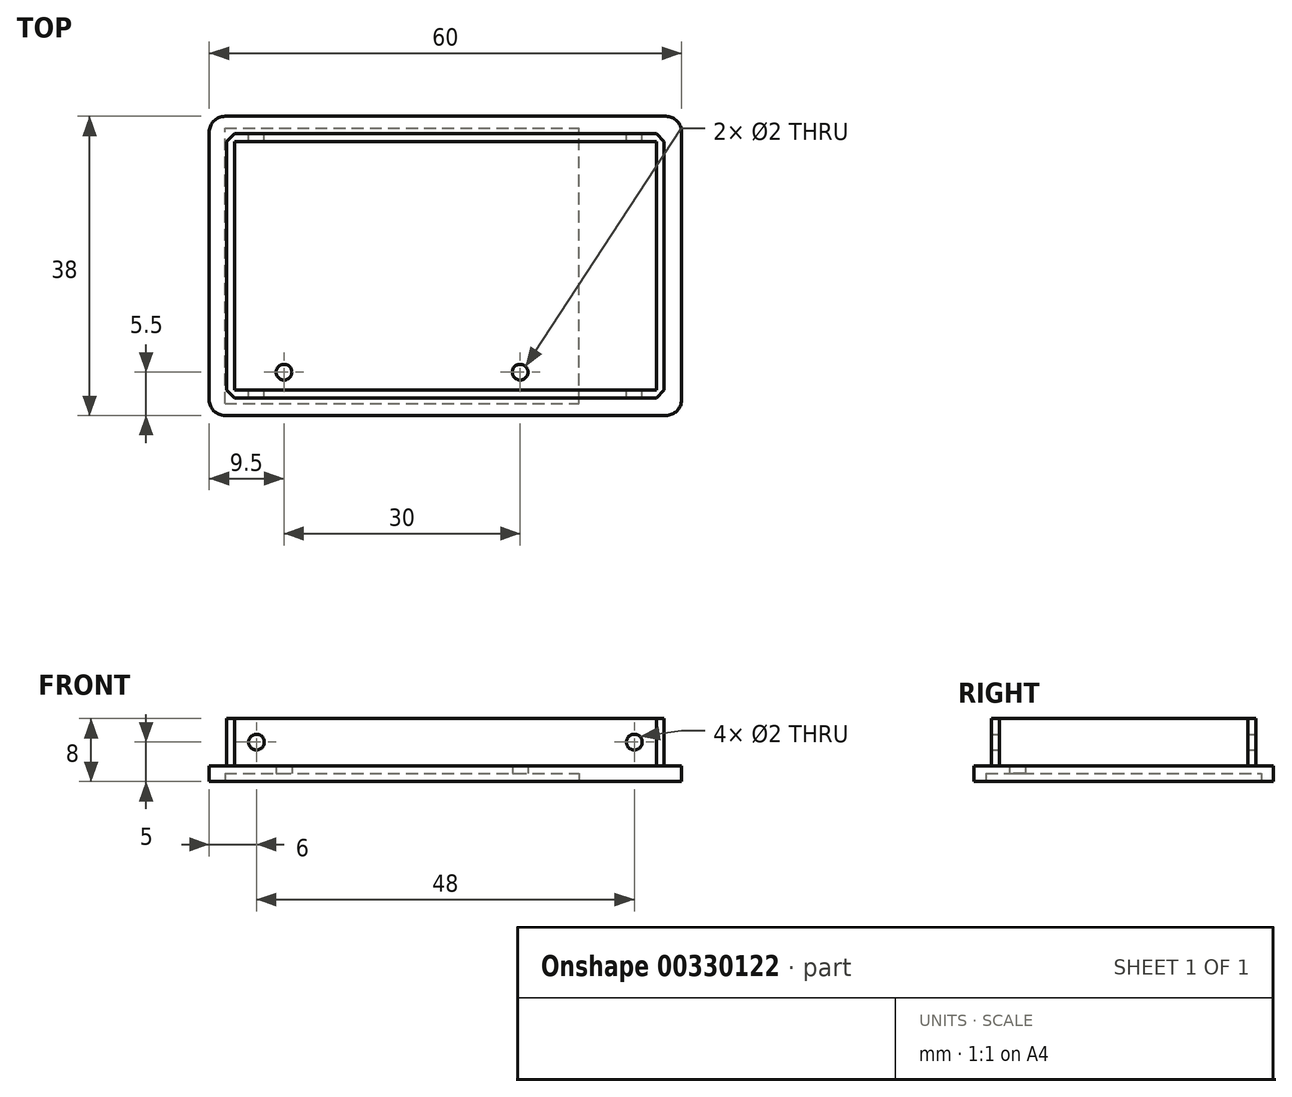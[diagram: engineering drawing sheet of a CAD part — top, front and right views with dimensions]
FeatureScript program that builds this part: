
annotation { "Feature Type Name" : "Feature", "Feature Type Description" : "" }
export const myFeature = defineFeature(function(context is Context, id is Id, definition is map)
    precondition{}
    {
        {
            var Q0;
            Q0=qCreatedBy(makeId("Top.planeOp"),FACE);
            var sketch = newSketch(context, id + "F0", { "sketchPlane" : qUnion([Q0])});
            skLineSegment(sketch, "E0.bottom", {"start": v(0, 0) * mm, "end": v(60, 0) * mm});
            skLineSegment(sketch, "E0.top", {"start": v(0, -38) * mm, "end": v(60, -38) * mm});
            skLineSegment(sketch, "E0.left", {"start": v(0, 0) * mm, "end": v(0, -38) * mm});
            skLineSegment(sketch, "E0.right", {"start": v(60, 0) * mm, "end": v(60, -38) * mm});
            skSolve(sketch);
        }
        {
            var Q0;
            Q0=qSketchRegion(id+"F0",true);
            extrude(context, id + "F1", {"entities" : qUnion([Q0]), "depth" : 2 * mm});
        }
        {
            var Q0;
            Q0=makeQuery(id+"F1.opExtrude","CAP_FACE",FACE,{"disambiguationData":[OSD([sQuery(id+"F0.wireOp",EDGE,"E0.bottom"),sQuery(id+"F0.wireOp",EDGE,"E0.top"),sQuery(id+"F0.wireOp",EDGE,"E0.left"),sQuery(id+"F0.wireOp",EDGE,"E0.right")])],"isStart":false});
            var sketch = newSketch(context, id + "F2", { "sketchPlane" : qUnion([Q0])});
            skLineSegment(sketch, "E1.bottom", {"start": v(2.2, -2.2) * mm, "end": v(57.8, -2.2) * mm});
            skLineSegment(sketch, "E1.top", {"start": v(2.2, -35.8) * mm, "end": v(57.8, -35.8) * mm});
            skLineSegment(sketch, "E1.left", {"start": v(2.2, -2.2) * mm, "end": v(2.2, -35.8) * mm});
            skLineSegment(sketch, "E1.right", {"start": v(57.8, -2.2) * mm, "end": v(57.8, -35.8) * mm});
            skLineSegment(sketch, "E2.bottom", {"start": v(3.2, -3.2) * mm, "end": v(56.8, -3.2) * mm});
            skLineSegment(sketch, "E2.top", {"start": v(3.2, -34.8) * mm, "end": v(56.8, -34.8) * mm});
            skLineSegment(sketch, "E2.left", {"start": v(3.2, -3.2) * mm, "end": v(3.2, -34.8) * mm});
            skLineSegment(sketch, "E2.right", {"start": v(56.8, -3.2) * mm, "end": v(56.8, -34.8) * mm});
            skSolve(sketch);
        }
        {
            var Q0;
            Q0=qSketchRegion(id+"F2",true);
            extrude(context, id + "F3", {"entities" : qUnion([Q0]), "operationType" : NewBodyOperationType.ADD, "depth" : 6 * mm});
        }
        {
            var Q0;
            Q0=makeQuery(id+"F1.opExtrude","CAP_FACE",FACE,{"disambiguationData":[OSD([sQuery(id+"F0.wireOp",EDGE,"E0.bottom"),sQuery(id+"F0.wireOp",EDGE,"E0.top"),sQuery(id+"F0.wireOp",EDGE,"E0.left"),sQuery(id+"F0.wireOp",EDGE,"E0.right")])],"isStart":true});
            var sketch = newSketch(context, id + "F4", { "sketchPlane" : qUnion([Q0])});
            skLineSegment(sketch, "E3.bottom", {"start": v(2, 36.5) * mm, "end": v(47, 36.5) * mm});
            skLineSegment(sketch, "E3.top", {"start": v(2, 1.5) * mm, "end": v(47, 1.5) * mm});
            skLineSegment(sketch, "E3.left", {"start": v(2, 36.5) * mm, "end": v(2, 1.5) * mm});
            skLineSegment(sketch, "E3.right", {"start": v(47, 36.5) * mm, "end": v(47, 1.5) * mm});
            skSolve(sketch);
        }
        {
            var Q0;
            Q0=qSketchRegion(id+"F4",true);
            extrude(context, id + "F5", {"entities" : qUnion([Q0]), "operationType" : NewBodyOperationType.REMOVE, "oppositeDirection" : true, "depth" : 1 * mm});
        }
        {
            var Q0;
            Q0=makeQuery(id+"F1.opExtrude","SWEPT_EDGE",EDGE,{"disambiguationData":[OSD([sQuery(id+"F0.wireOp",EDGE,"E0.top"),sQuery(id+"F0.wireOp",EDGE,"E0.left")])]});
            var Q1;
            Q1=makeQuery(id+"F1.opExtrude","SWEPT_EDGE",EDGE,{"disambiguationData":[OSD([sQuery(id+"F0.wireOp",EDGE,"E0.bottom"),sQuery(id+"F0.wireOp",EDGE,"E0.left")])]});
            var Q2;
            Q2=makeQuery(id+"F1.opExtrude","SWEPT_EDGE",EDGE,{"disambiguationData":[OSD([sQuery(id+"F0.wireOp",EDGE,"E0.top"),sQuery(id+"F0.wireOp",EDGE,"E0.right")])]});
            var Q3;
            Q3=makeQuery(id+"F1.opExtrude","SWEPT_EDGE",EDGE,{"disambiguationData":[OSD([sQuery(id+"F0.wireOp",EDGE,"E0.bottom"),sQuery(id+"F0.wireOp",EDGE,"E0.right")])]});
            fillet(context, id + "F6", {"entities" : qUnion([Q0, Q1, Q2, Q3]), "radius" : 2 * mm, "tangentPropagation" : true, "allowEdgeOverflow" : false});
        }
        {
            var Q0;
            Q0=makeQuery(id+"F1.opExtrude","CAP_FACE",FACE,{"disambiguationData":[OSD([sQuery(id+"F0.wireOp",EDGE,"E0.bottom"),sQuery(id+"F0.wireOp",EDGE,"E0.top"),sQuery(id+"F0.wireOp",EDGE,"E0.left"),sQuery(id+"F0.wireOp",EDGE,"E0.right")])],"isStart":true});
            var sketch = newSketch(context, id + "F7", { "sketchPlane" : qUnion([Q0])});
            skCircle(sketch, "E4", {"center": v(9.5, 32.5) * mm, "radius": 1 * mm});
            skCircle(sketch, "E5", {"center": v(39.5, 32.5) * mm, "radius": 1 * mm});
            skSolve(sketch);
        }
        {
            var Q0;
            Q0 = qSketchRegion(id + "F7", true);
            extrude(context, id + "F8", {"entities" : qUnion([Q0]), "operationType" : NewBodyOperationType.REMOVE, "endBound" : BoundingType.THROUGH_ALL, "oppositeDirection" : true, "depth" : 25 * mm});
        }
        {
            var Q0;
            Q0=makeQuery(id+"F3.opExtrude","SWEPT_FACE",FACE,{"disambiguationData":[OSD([sQuery(id+"F2.wireOp",EDGE,"E1.bottom")])]});
            var sketch = newSketch(context, id + "F9", { "sketchPlane" : qUnion([Q0])});
            skCircle(sketch, "E6", {"center": v(-54, 5) * mm, "radius": 1 * mm});
            skCircle(sketch, "E7", {"center": v(-6, 5) * mm, "radius": 1 * mm});
            skSolve(sketch);
        }
        {
            var Q0;
            Q0 = qSketchRegion(id + "F9", true);
            extrude(context, id + "F10", {"entities" : qUnion([Q0]), "operationType" : NewBodyOperationType.REMOVE, "endBound" : BoundingType.THROUGH_ALL, "oppositeDirection" : true, "depth" : 25 * mm});
        }
        {
            var Q0;
            Q0=makeQuery(id+"F3.opExtrude","SWEPT_EDGE",EDGE,{"disambiguationData":[OSD([sQuery(id+"F2.wireOp",EDGE,"E1.bottom"),sQuery(id+"F2.wireOp",EDGE,"E1.left")])]});
            var Q1;
            Q1=makeQuery(id+"F3.opExtrude","SWEPT_EDGE",EDGE,{"disambiguationData":[OSD([sQuery(id+"F2.wireOp",EDGE,"E1.top"),sQuery(id+"F2.wireOp",EDGE,"E1.left")])]});
            var Q2;
            Q2=makeQuery(id+"F3.opExtrude","SWEPT_EDGE",EDGE,{"disambiguationData":[OSD([sQuery(id+"F2.wireOp",EDGE,"E1.top"),sQuery(id+"F2.wireOp",EDGE,"E1.right")])]});
            var Q3;
            Q3=makeQuery(id+"F3.opExtrude","SWEPT_EDGE",EDGE,{"disambiguationData":[OSD([sQuery(id+"F2.wireOp",EDGE,"E1.bottom"),sQuery(id+"F2.wireOp",EDGE,"E1.right")])]});
            chamfer(context, id + "F11", {"entities" : qUnion([Q0, Q1, Q2, Q3]), "width" : 1 * mm, "tangentPropagation" : true});
        }
    });
